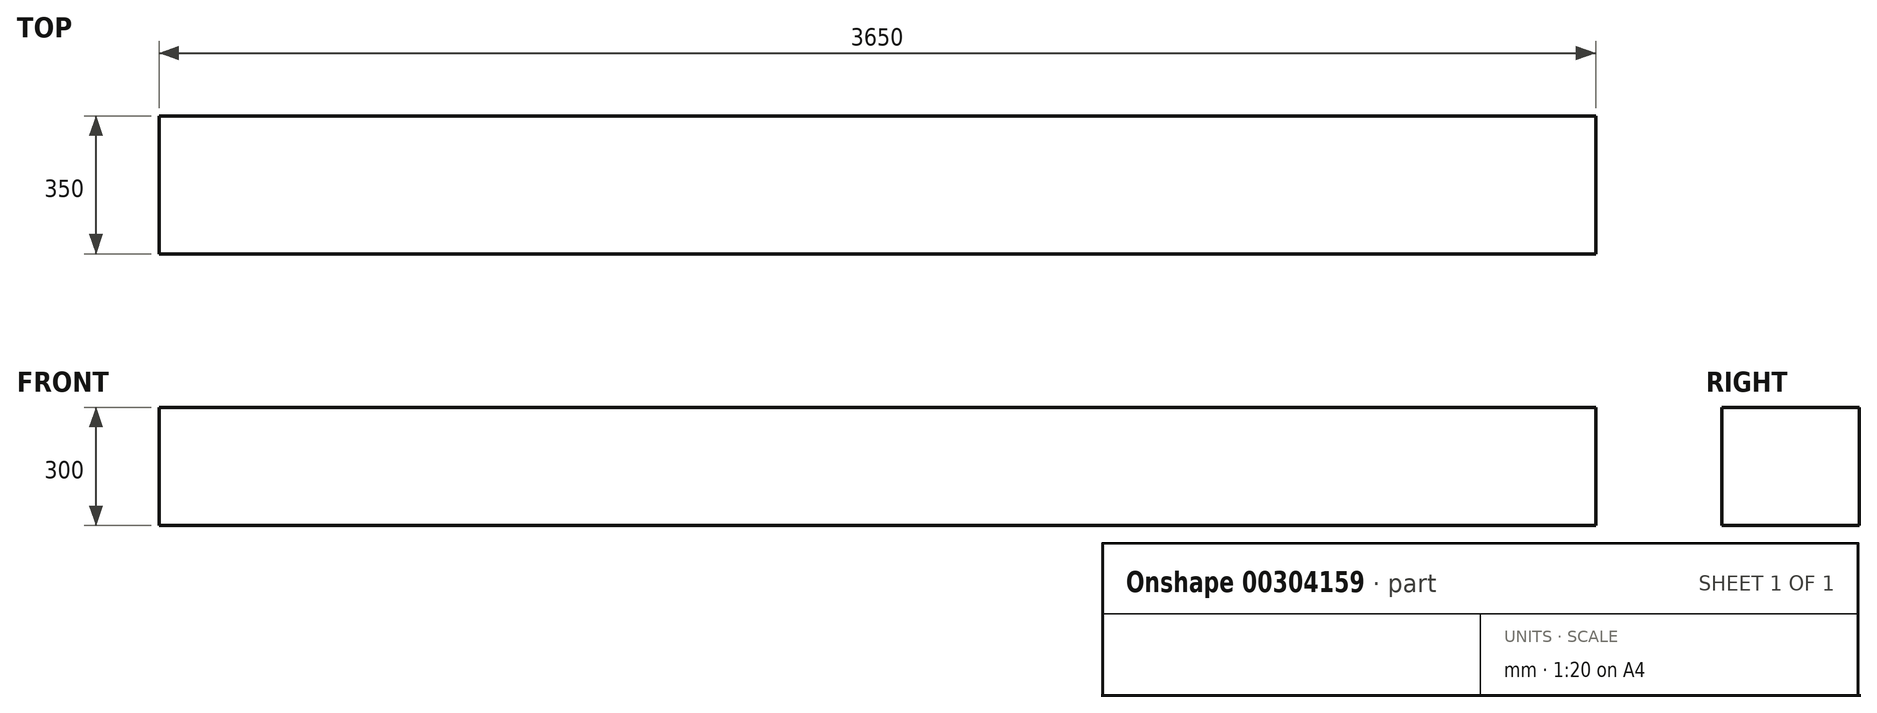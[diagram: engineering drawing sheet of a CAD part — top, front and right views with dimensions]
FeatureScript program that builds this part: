
annotation { "Feature Type Name" : "Feature", "Feature Type Description" : "" }
export const myFeature = defineFeature(function(context is Context, id is Id, definition is map)
    precondition{}
    {
        {
            var Q0;
            Q0=qCreatedBy(makeId("Top.planeOp"),FACE);
            var sketch = newSketch(context, id + "F0", { "sketchPlane" : qUnion([Q0])});
            skLineSegment(sketch, "E0.bottom", {"start": v(-1819.87, -5.85) * mm, "end": v(1830.13, -5.85) * mm});
            skLineSegment(sketch, "E0.top", {"start": v(-1819.87, -355.85) * mm, "end": v(1830.13, -355.85) * mm});
            skLineSegment(sketch, "E0.left", {"start": v(-1819.87, -5.85) * mm, "end": v(-1819.87, -355.85) * mm});
            skLineSegment(sketch, "E0.right", {"start": v(1830.13, -5.85) * mm, "end": v(1830.13, -355.85) * mm});
            skSolve(sketch);
        }
        {
            var Q0;
            Q0=makeQuery(id+"F0.imprint","IMPRINT",FACE,{"disambiguationData":[TD([[makeQuery(id+"F0.imprint","IMPRINT",EDGE,{"derivedFrom":sQuery(id+"F0.wireOp",EDGE,"E0.bottom")}),-1.0]])]});
            extrude(context, id + "F1", {"entities" : qUnion([Q0]), "depth" : 300 * mm});
        }
    });
